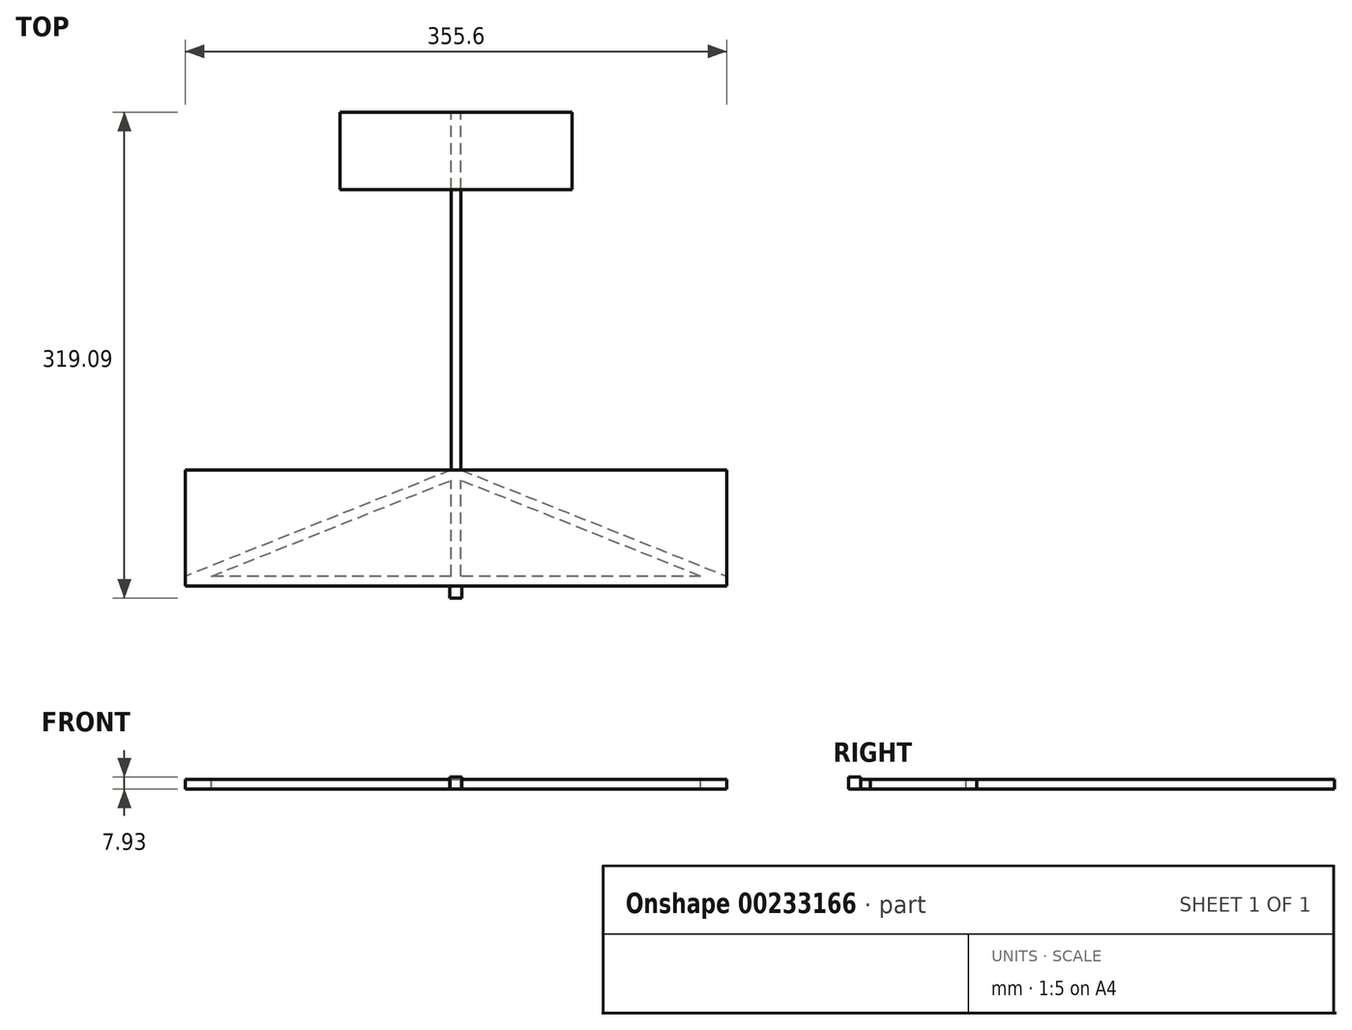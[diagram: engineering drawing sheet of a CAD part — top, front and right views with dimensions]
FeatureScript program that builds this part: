
annotation { "Feature Type Name" : "Feature", "Feature Type Description" : "" }
export const myFeature = defineFeature(function(context is Context, id is Id, definition is map)
    precondition{}
    {
        {
            var Q0;
            Q0=qCreatedBy(makeId("Front.planeOp"),FACE);
            var sketch = newSketch(context, id + "F0", { "sketchPlane" : qUnion([Q0])});
            skLineSegment(sketch, "E0.bottom", {"start": v(3.18, 3.17) * mm, "end": v(-3.18, 3.17) * mm});
            skLineSegment(sketch, "E0.top", {"start": v(3.18, -3.18) * mm, "end": v(-3.18, -3.18) * mm});
            skLineSegment(sketch, "E0.left", {"start": v(3.17, 3.17) * mm, "end": v(3.18, -3.18) * mm});
            skLineSegment(sketch, "E0.right", {"start": v(-3.18, 3.17) * mm, "end": v(-3.18, -3.18) * mm});
            skPoint(sketch, "E0.middle", {"position": v(0, 0) * mm});
            skSolve(sketch);
        }
        {
            var Q0;
            Q0=makeQuery(id+"F0.imprint","IMPRINT",FACE,{"disambiguationData":[TD([[makeQuery(id+"F0.imprint","IMPRINT",EDGE,{"derivedFrom":sQuery(id+"F0.wireOp",EDGE,"E0.bottom")}),1.0]])]});
            extrude(context, id + "F1", {"entities" : qUnion([Q0]), "depth" : 304.8 * mm});
        }
        {
            var Q0;
            Q0=makeQuery(id+"F1.opExtrude","SWEPT_FACE",FACE,{"disambiguationData":[OSD([sQuery(id+"F0.wireOp",EDGE,"E0.bottom")])]});
            var sketch = newSketch(context, id + "F2", { "sketchPlane" : qUnion([Q0])});
            skLineSegment(sketch, "E1.bottom", {"start": v(76.2, -50.8) * mm, "end": v(-76.2, -50.8) * mm});
            skLineSegment(sketch, "E1.top", {"start": v(76.2, 0) * mm, "end": v(-76.2, 0) * mm});
            skLineSegment(sketch, "E1.left", {"start": v(76.2, -50.8) * mm, "end": v(76.2, 0) * mm});
            skLineSegment(sketch, "E1.right", {"start": v(-76.2, -50.8) * mm, "end": v(-76.2, 0) * mm});
            skPoint(sketch, "E1.middle", {"position": v(0, -25.4) * mm});
            skSolve(sketch);
        }
        {
            var Q0;
            {var subQ0=sQuery(id+"F2.wireOp",EDGE,"E1.left");Q0=makeQuery(id+"F2.imprint","IMPRINT",FACE,{"disambiguationData":[TD([[makeQuery(id+"F2.imprint","IMPRINT",EDGE,{"derivedFrom":subQ0}),1.0]])]});}
            var Q1;
            {var subQ0=sQuery(id+"F2.wireOp",EDGE,"E1.right");Q1=makeQuery(id+"F2.imprint","IMPRINT",FACE,{"disambiguationData":[TD([[makeQuery(id+"F2.imprint","IMPRINT",EDGE,{"derivedFrom":subQ0}),-1.0]])]});}
            var Q2;
            {var subQ0=sQuery(id+"F2.wireOp",EDGE,"E1.bottom");var subQ1=sQuery(id+"F0.wireOp",EDGE,"E0.bottom");var subQ2=makeQuery(id+"F1.opExtrude","SWEPT_EDGE",EDGE,{"disambiguationData":[OSD([subQ1,sQuery(id+"F0.wireOp",EDGE,"E0.left")])]});var subQ3=makeQuery(id+"F2.imprint","INTERSECT",VERTEX,{"derivedFrom":[subQ2,subQ0]});Q2=makeQuery(id+"F2.imprint","IMPRINT",FACE,{"disambiguationData":[TD([[makeQuery(id+"F2.imprint","IMPRINT",EDGE,{"disambiguationData":[TD([[subQ3,-1.0]])],"derivedFrom":subQ0}),-1.0]])]});}
            extrude(context, id + "F3", {"entities" : qUnion([Q0, Q1, Q2]), "operationType" : NewBodyOperationType.ADD, "depth" : 1 / 406.4 * mm});
        }
        {
            var Q0;
            Q0=makeQuery(id+"F1.opExtrude","SWEPT_FACE",FACE,{"disambiguationData":[OSD([sQuery(id+"F0.wireOp",EDGE,"E0.bottom")])]});
            var sketch = newSketch(context, id + "F4", { "sketchPlane" : qUnion([Q0])});
            skLineSegment(sketch, "E2.bottom", {"start": v(-177.8, -234.95) * mm, "end": v(177.8, -234.95) * mm});
            skLineSegment(sketch, "E2.top", {"start": v(-177.8, -311.15) * mm, "end": v(177.8, -311.15) * mm});
            skLineSegment(sketch, "E2.left", {"start": v(-177.8, -234.95) * mm, "end": v(-177.8, -311.15) * mm});
            skLineSegment(sketch, "E2.right", {"start": v(177.8, -234.95) * mm, "end": v(177.8, -311.15) * mm});
            skPoint(sketch, "E2.middle", {"position": v(0, -273.05) * mm});
            skPoint(sketch, "E2.middle.positionSnap0", {"position": v(0, -304.8) * mm});
            skPoint(sketch, "E2.centerSnap0", {"position": v(0, -304.8) * mm});
            skSolve(sketch);
        }
        {
            var Q0;
            {var subQ0=sQuery(id+"F4.wireOp",EDGE,"E2.left");Q0=makeQuery(id+"F4.imprint","IMPRINT",FACE,{"disambiguationData":[TD([[makeQuery(id+"F4.imprint","IMPRINT",EDGE,{"derivedFrom":subQ0}),1.0]])]});}
            var Q1;
            {var subQ0=sQuery(id+"F4.wireOp",EDGE,"E2.right");Q1=makeQuery(id+"F4.imprint","IMPRINT",FACE,{"disambiguationData":[TD([[makeQuery(id+"F4.imprint","IMPRINT",EDGE,{"derivedFrom":subQ0}),-1.0]])]});}
            var Q2;
            {var subQ0=sQuery(id+"F4.wireOp",EDGE,"E2.bottom");var subQ1=sQuery(id+"F0.wireOp",EDGE,"E0.right");var subQ4=sQuery(id+"F0.wireOp",EDGE,"E0.left");var subQ5=sQuery(id+"F0.wireOp",EDGE,"E0.bottom");var subQ6=makeQuery(id+"F1.opExtrude","CAP_FACE",FACE,{"disambiguationData":[OSD([subQ5,sQuery(id+"F0.wireOp",EDGE,"E0.top"),subQ4,subQ1])],"isStart":false});var subQ9=makeQuery(id+"F3.boolean.opBoolean","SPLIT",EDGE,{"disambiguationData":[TD([subQ6])],"derivedFrom":makeQuery(id+"F1.opExtrude","SWEPT_EDGE",EDGE,{"disambiguationData":[OSD([subQ5,subQ1])]})});var subQ10=makeQuery(id+"F4.imprint","INTERSECT",VERTEX,{"derivedFrom":[subQ9,subQ0]});Q2=makeQuery(id+"F4.imprint","IMPRINT",FACE,{"disambiguationData":[TD([[makeQuery(id+"F4.imprint","IMPRINT",EDGE,{"disambiguationData":[TD([[subQ10,-1.0]])],"derivedFrom":subQ0}),-1.0]])]});}
            extrude(context, id + "F5", {"entities" : qUnion([Q0, Q1, Q2]), "operationType" : NewBodyOperationType.ADD, "depth" : 1 / 406.4 * mm});
        }
        {
            var Q0;
            Q0=makeQuery(id+"F5.opExtrude","CAP_FACE",FACE,{"disambiguationData":[OSD([sQuery(id+"F4.wireOp",EDGE,"E2.bottom"),sQuery(id+"F4.wireOp",EDGE,"E2.top"),sQuery(id+"F4.wireOp",EDGE,"E2.left"),sQuery(id+"F4.wireOp",EDGE,"E2.right")])],"isStart":true});
            var sketch = newSketch(context, id + "F6", { "sketchPlane" : qUnion([Q0])});
            skLineSegment(sketch, "E3.bottom", {"start": v(-177.8, 304.8) * mm, "end": v(177.8, 304.8) * mm});
            skLineSegment(sketch, "E3.top", {"start": v(-177.8, 311.15) * mm, "end": v(177.8, 311.15) * mm});
            skLineSegment(sketch, "E3.left", {"start": v(-177.8, 304.8) * mm, "end": v(-177.8, 311.15) * mm});
            skLineSegment(sketch, "E3.right", {"start": v(177.8, 304.8) * mm, "end": v(177.8, 311.15) * mm});
            skPoint(sketch, "E3.middle", {"position": v(0, 307.97) * mm});
            skPoint(sketch, "E3.middle.positionSnap0", {"position": v(0, 311.15) * mm});
            skPoint(sketch, "E3.centerSnap0", {"position": v(0, 311.15) * mm});
            skSolve(sketch);
        }
        {
            var Q0;
            Q0=makeQuery(id+"F6.imprint","IMPRINT",FACE,{"disambiguationData":[TD([[makeQuery(id+"F6.imprint","IMPRINT",EDGE,{"derivedFrom":sQuery(id+"F6.wireOp",EDGE,"E3.top")}),-1.0]])]});
            extrude(context, id + "F7", {"entities" : qUnion([Q0]), "operationType" : NewBodyOperationType.ADD, "depth" : 6.35 * mm});
        }
        {
            var Q0;
            {var subQ0=sQuery(id+"F4.wireOp",EDGE,"E2.left");var subQ1=sQuery(id+"F4.wireOp",EDGE,"E2.bottom");Q0=makeQuery(id+"F7.boolean.opBoolean","SPLIT",FACE,{"disambiguationData":[TD([makeQuery(id+"F1.opExtrude","SWEPT_FACE",FACE,{"disambiguationData":[OSD([sQuery(id+"F0.wireOp",EDGE,"E0.right")])]})])],"derivedFrom":makeQuery(id+"F5.opExtrude","CAP_FACE",FACE,{"disambiguationData":[OSD([subQ1,sQuery(id+"F4.wireOp",EDGE,"E2.top"),subQ0,sQuery(id+"F4.wireOp",EDGE,"E2.right")])],"isStart":true})});}
            var sketch = newSketch(context, id + "F8", { "sketchPlane" : qUnion([Q0])});
            skLineSegment(sketch, "E4", {"start": v(-3.18, 234.95) * mm, "end": v(-177.8, 304.8) * mm});
            skLineSegment(sketch, "E5", {"start": v(-177.8, 304.8) * mm, "end": v(-160.7, 304.8) * mm});
            skLineSegment(sketch, "E6", {"start": v(-160.7, 304.8) * mm, "end": v(-3.18, 241.79) * mm});
            skLineSegment(sketch, "E7", {"start": v(-3.18, 241.79) * mm, "end": v(-3.18, 234.95) * mm});
            skLineSegment(sketch, "E8", {"start": v(0, 226.84) * mm, "end": v(0, 226.84) * mm});
            skSolve(sketch);
        }
        {
            var Q0;
            Q0=makeQuery(id+"F8.imprint","IMPRINT",FACE,{"disambiguationData":[TD([[makeQuery(id+"F8.imprint","IMPRINT",EDGE,{"derivedFrom":sQuery(id+"F8.wireOp",EDGE,"E4")}),-1.0]])]});
            extrude(context, id + "F9", {"entities" : qUnion([Q0]), "operationType" : NewBodyOperationType.ADD, "depth" : 6.35 * mm});
        }
        {
            var Q0;
            Q0=makeQuery(id+"F1.opExtrude","SWEPT_BODY",BODY,{"disambiguationData":[OSD([sQuery(id+"F0.wireOp",EDGE,"E0.bottom"),sQuery(id+"F0.wireOp",EDGE,"E0.top"),sQuery(id+"F0.wireOp",EDGE,"E0.left"),sQuery(id+"F0.wireOp",EDGE,"E0.right")])]});
            var Q1;
            Q1=qCreatedBy(makeId("Right.planeOp"),FACE);
            mirror(context, id + "F10", {"operationType" : NewBodyOperationType.ADD, "entities" : qUnion([Q0]), "mirrorPlane" : qUnion([Q1])});
        }
        {
            var Q0;
            Q0=makeQuery(id+"F7.boolean.opBoolean","MERGE",FACE,{"derivedFrom":[makeQuery(id+"F5.opExtrude","SWEPT_FACE",FACE,{"disambiguationData":[OSD([sQuery(id+"F4.wireOp",EDGE,"E2.top")])]}),makeQuery(id+"F7.opExtrude","SWEPT_FACE",FACE,{"disambiguationData":[OSD([sQuery(id+"F6.wireOp",EDGE,"E3.top")])]})]});
            var sketch = newSketch(context, id + "F11", { "sketchPlane" : qUnion([Q0])});
            skLineSegment(sketch, "E9.bottom", {"start": v(3.97, 4.76) * mm, "end": v(-3.97, 4.76) * mm});
            skLineSegment(sketch, "E9.top", {"start": v(3.97, -3.18) * mm, "end": v(-3.97, -3.18) * mm});
            skLineSegment(sketch, "E9.left", {"start": v(3.97, 4.76) * mm, "end": v(3.97, -3.17) * mm});
            skLineSegment(sketch, "E9.right", {"start": v(-3.97, 4.76) * mm, "end": v(-3.97, -3.18) * mm});
            skPoint(sketch, "E9.middle", {"position": v(0, 0) * mm});
            skSolve(sketch);
        }
        {
            var Q0;
            Q0 = qSketchRegion(id + "F11", true);
            extrude(context, id + "F12", {"entities" : qUnion([Q0]), "depth" : 7.94 * mm});
        }
    });
